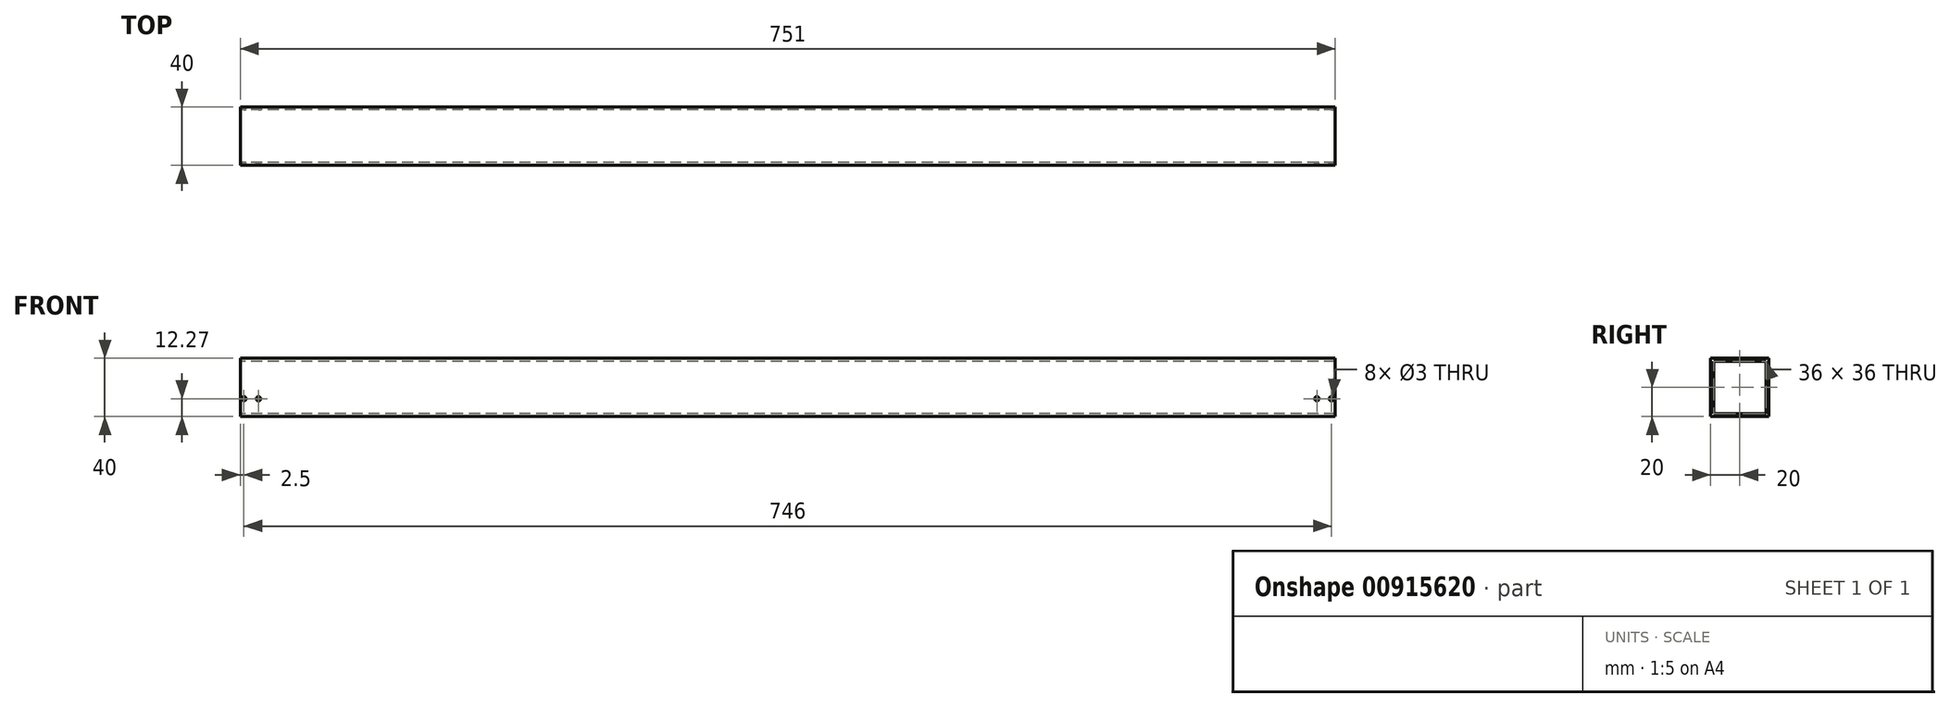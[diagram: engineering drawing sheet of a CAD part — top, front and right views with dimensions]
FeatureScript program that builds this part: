
annotation { "Feature Type Name" : "Feature", "Feature Type Description" : "" }
export const myFeature = defineFeature(function(context is Context, id is Id, definition is map)
    precondition{}
    {
        {
            var Q0;
            Q0=qCreatedBy(makeId("Right.planeOp"),FACE);
            var sketch = newSketch(context, id + "F0", { "sketchPlane" : qUnion([Q0])});
            skLineSegment(sketch, "E0.bottom", {"start": v(20, -20) * mm, "end": v(-20, -20) * mm});
            skLineSegment(sketch, "E0.top", {"start": v(20, 20) * mm, "end": v(-20, 20) * mm});
            skLineSegment(sketch, "E0.left", {"start": v(20, -20) * mm, "end": v(20, 20) * mm});
            skLineSegment(sketch, "E0.right", {"start": v(-20, -20) * mm, "end": v(-20, 20) * mm});
            skPoint(sketch, "E0.middle", {"position": v(0, 0) * mm});
            skLineSegment(sketch, "E1.bottom", {"start": v(18, -18) * mm, "end": v(-18, -18) * mm});
            skLineSegment(sketch, "E1.top", {"start": v(18, 18) * mm, "end": v(-18, 18) * mm});
            skLineSegment(sketch, "E1.left", {"start": v(18, -18) * mm, "end": v(18, 18) * mm});
            skLineSegment(sketch, "E1.right", {"start": v(-18, -18) * mm, "end": v(-18, 18) * mm});
            skSolve(sketch);
        }
        {
            var Q0;
            Q0=makeQuery(id+"F0.imprint","IMPRINT",FACE,{"disambiguationData":[TD([[makeQuery(id+"F0.imprint","IMPRINT",EDGE,{"derivedFrom":sQuery(id+"F0.wireOp",EDGE,"E0.bottom")}),-1.0]])]});
            extrude(context, id + "F1", {"entities" : qUnion([Q0]), "depth" : 751 * mm, "offsetDistance" : 25 * mm});
        }
        {
            var Q0;
            Q0=makeQuery(id+"F1.opExtrude","SWEPT_FACE",FACE,{"disambiguationData":[OSD([sQuery(id+"F0.wireOp",EDGE,"E0.left")])]});
            var sketch = newSketch(context, id + "F2", { "sketchPlane" : qUnion([Q0])});
            skLineSegment(sketch, "E2", {"start": v(0, -7.73) * mm, "end": v(-2.5, -7.73) * mm});
            skLineSegment(sketch, "E3", {"start": v(-2.5, -7.73) * mm, "end": v(-12.5, -7.73) * mm});
            skLineSegment(sketch, "E4", {"start": v(-751, -7.73) * mm, "end": v(-748.5, -7.73) * mm});
            skLineSegment(sketch, "E5", {"start": v(-748.5, -7.73) * mm, "end": v(-738.5, -7.73) * mm});
            skSolve(sketch);
        }
        {
            var Q0;
            Q0=sQuery(id+"F2.wireOp",VERTEX,"E4.end");
            var Q1;
            Q1=sQuery(id+"F2.wireOp",VERTEX,"E5.end");
            var Q2;
            Q2=sQuery(id+"F2.wireOp",VERTEX,"E2.end");
            var Q3;
            Q3=sQuery(id+"F2.wireOp",VERTEX,"E3.end");
            var Q4;
            Q4=makeQuery(id+"F1.opExtrude","SWEPT_BODY",BODY,{"disambiguationData":[OSD([sQuery(id+"F0.wireOp",EDGE,"E0.bottom"),sQuery(id+"F0.wireOp",EDGE,"E0.top"),sQuery(id+"F0.wireOp",EDGE,"E0.left"),sQuery(id+"F0.wireOp",EDGE,"E0.right"),sQuery(id+"F0.wireOp",EDGE,"E1.bottom"),sQuery(id+"F0.wireOp",EDGE,"E1.top"),sQuery(id+"F0.wireOp",EDGE,"E1.left"),sQuery(id+"F0.wireOp",EDGE,"E1.right")])]});
            hole(context, id + "F3", {"style" : HoleStyle.SIMPLE, "endStyle" : HoleEndStyle.BLIND, "holeDiameter" : 3 * mm, "majorDiameter" : 5 * mm, "holeDepth" : 50 * mm, "isTappedThrough" : true, "tappedDepth" : 12 * mm, "tapClearance" : 3, "locations" : qUnion([Q0, Q1, Q2, Q3]), "scope" : qUnion([Q4])});
        }
    });
